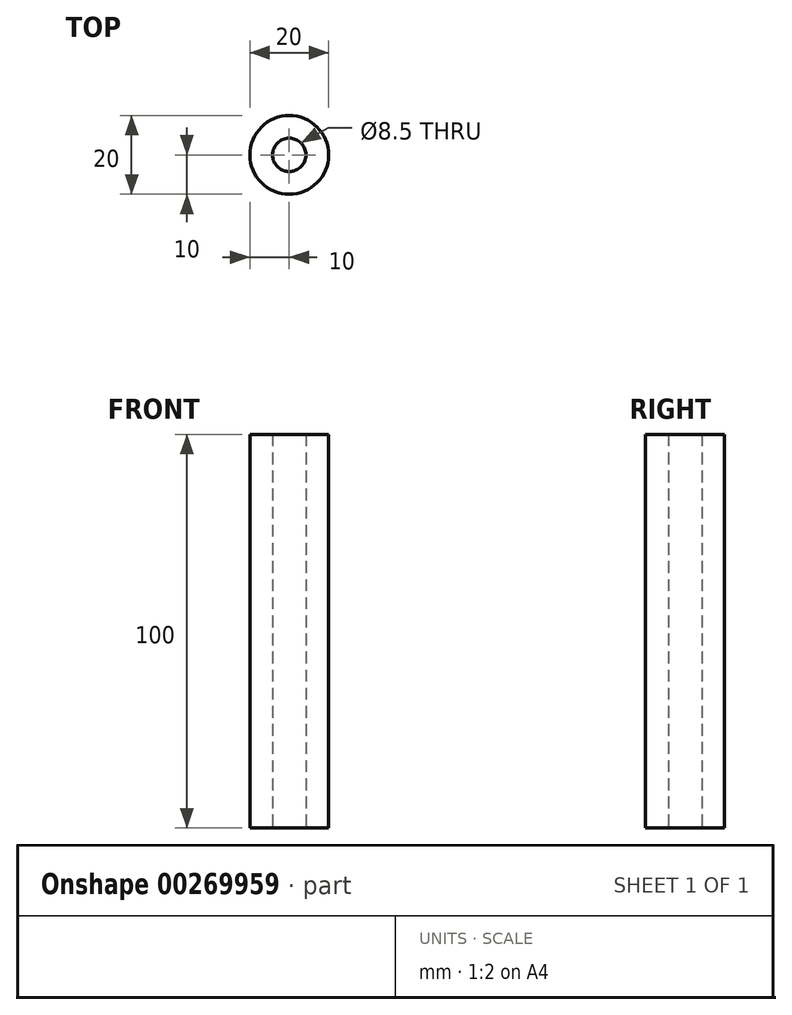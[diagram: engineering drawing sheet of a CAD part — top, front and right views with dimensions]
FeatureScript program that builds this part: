
annotation { "Feature Type Name" : "Feature", "Feature Type Description" : "" }
export const myFeature = defineFeature(function(context is Context, id is Id, definition is map)
    precondition{}
    {
        {
            var Q0;
            Q0=qCreatedBy(makeId("Top.planeOp"),FACE);
            var sketch = newSketch(context, id + "F0", { "sketchPlane" : qUnion([Q0])});
            skCircle(sketch, "E0", {"center": v(0, 0) * mm, "radius": 10 * mm});
            skCircle(sketch, "E1", {"center": v(0, 0) * mm, "radius": 4.25 * mm});
            skSolve(sketch);
        }
        {
            var Q0;
            Q0=makeQuery(id+"F0.imprint","IMPRINT",FACE,{"disambiguationData":[TD([[makeQuery(id+"F0.imprint","IMPRINT",EDGE,{"derivedFrom":sQuery(id+"F0.wireOp",EDGE,"E0")}),1.0]])]});
            extrude(context, id + "F1", {"entities" : qUnion([Q0]), "depth" : 100 * mm});
        }
    });
